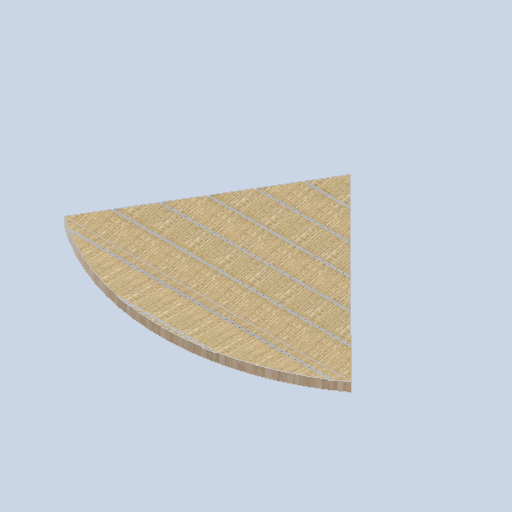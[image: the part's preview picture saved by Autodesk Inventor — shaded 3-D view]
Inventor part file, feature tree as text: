
AUTODESK INVENTOR PART (.ipt)
format: ipt  version: 2024.2 (Build 282272000, 272)  size: 277,504 bytes
history: native  units: in
note: dims shown in document units (in); Inventor stores cm internally (conversion verified against a paired STEP export)
features: sketch x11, plane x4, other x3
ambient origin geometry x8: Origin, YZ Plane, XZ Plane, XY Plane, X Axis, Y Axis, Z Axis, Center Point
bodies: Solid1 (feature_tree)
feature tree (18):
  other  "eave_panel_corner.ipt"
  other  "Solid1::eave_panel_corner.ipt"
  other  "TaggingFeature1"
  sketch  "Sketch1"  dims[d0=0.3937in]
  sketch  "Sketch2"
  sketch  "Sketch5"
  sketch  "Sketch6"
  sketch  "Sketch11"
  sketch  "Sketch12"
  sketch  "Sketch13"
  sketch  "Sketch14"
  sketch  "Sketch15"
  sketch  "Sketch16"
  sketch  "Sketch17"
  plane  "Work Plane1"
  plane  "Work Plane2"
  plane  "Work Plane3"
  plane  "Work Plane4"
